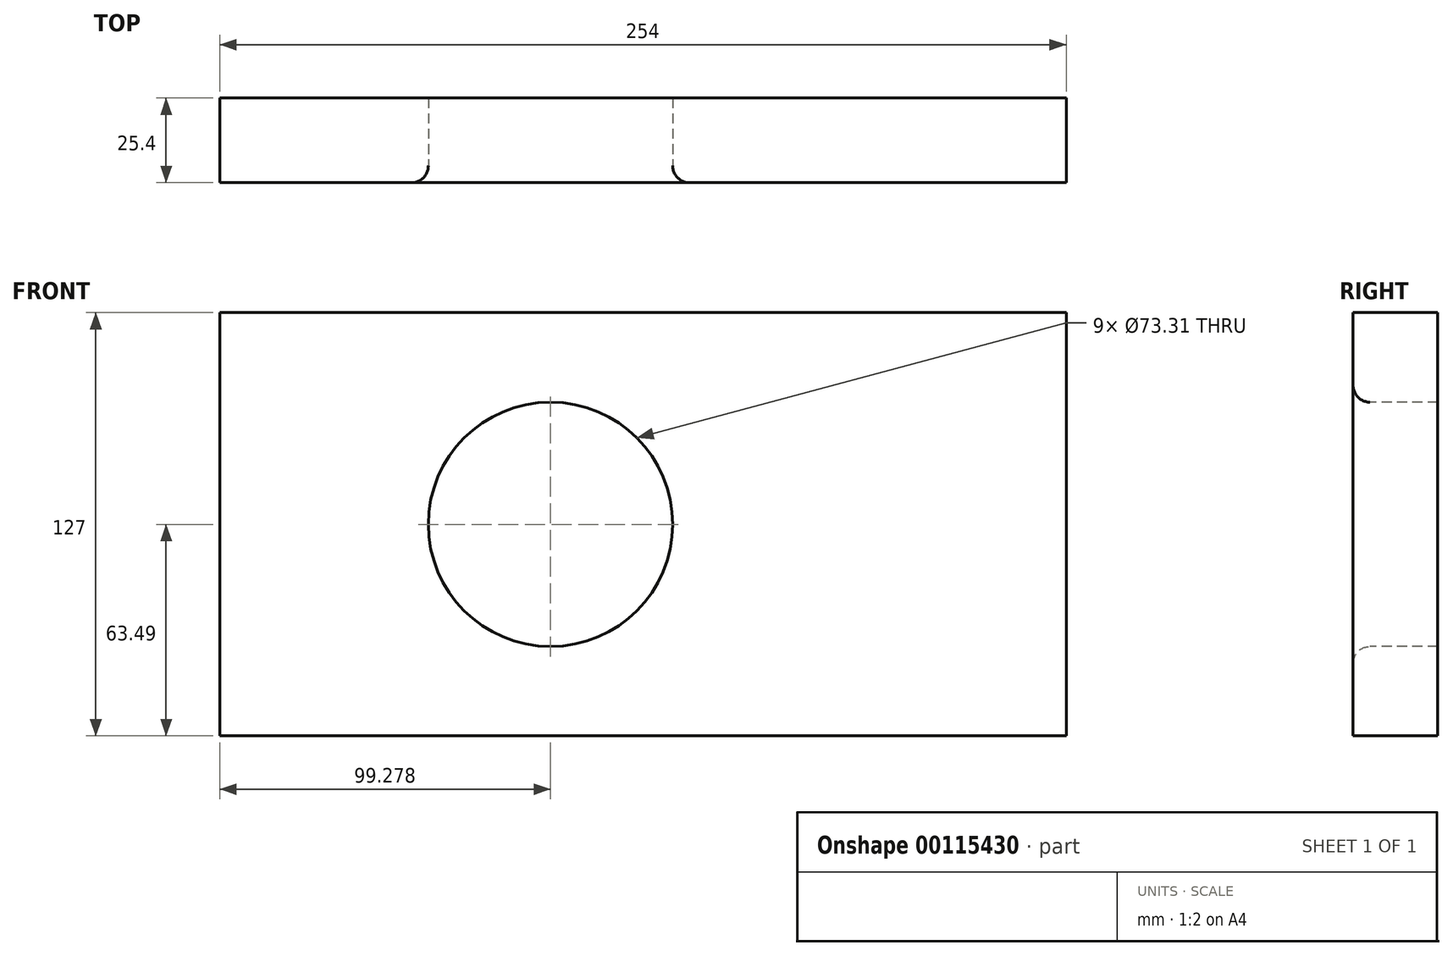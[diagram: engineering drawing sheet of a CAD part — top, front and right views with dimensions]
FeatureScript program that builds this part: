
annotation { "Feature Type Name" : "Feature", "Feature Type Description" : "" }
export const myFeature = defineFeature(function(context is Context, id is Id, definition is map)
    precondition{}
    {
        {
            var Q0;
            Q0=qCreatedBy(makeId("Front.planeOp"),FACE);
            var sketch = newSketch(context, id + "F0", { "sketchPlane" : qUnion([Q0])});
            skLineSegment(sketch, "E0.bottom", {"start": v(-276.7, 90.31) * mm, "end": v(-22.7, 90.31) * mm});
            skLineSegment(sketch, "E0.top", {"start": v(-276.7, -36.69) * mm, "end": v(-22.7, -36.69) * mm});
            skLineSegment(sketch, "E0.left", {"start": v(-276.7, 90.31) * mm, "end": v(-276.7, -36.69) * mm});
            skLineSegment(sketch, "E0.right", {"start": v(-22.7, 90.31) * mm, "end": v(-22.7, -36.69) * mm});
            skCircle(sketch, "E1", {"center": v(-177.42, 26.8) * mm, "radius": 36.66 * mm});
            skSolve(sketch);
        }
        {
            var Q0;
            Q0=makeQuery(id+"F0.imprint","IMPRINT",FACE,{"disambiguationData":[TD([[makeQuery(id+"F0.imprint","IMPRINT",EDGE,{"derivedFrom":sQuery(id+"F0.wireOp",EDGE,"E0.bottom")}),-1.0]])]});
            extrude(context, id + "F1", {"entities" : qUnion([Q0]), "oppositeDirection" : true, "depth" : 25.4 * mm});
        }
        {
            var Q0;
            Q0=makeQuery(id+"F1.opExtrude","CAP_EDGE",EDGE,{"disambiguationData":[OSD([sQuery(id+"F0.wireOp",EDGE,"E1")])],"isStart":true});
            fillet(context, id + "F2", {"entities" : qUnion([Q0]), "radius" : 5.08 * mm, "tangentPropagation" : true, "allowEdgeOverflow" : false});
        }
    });
